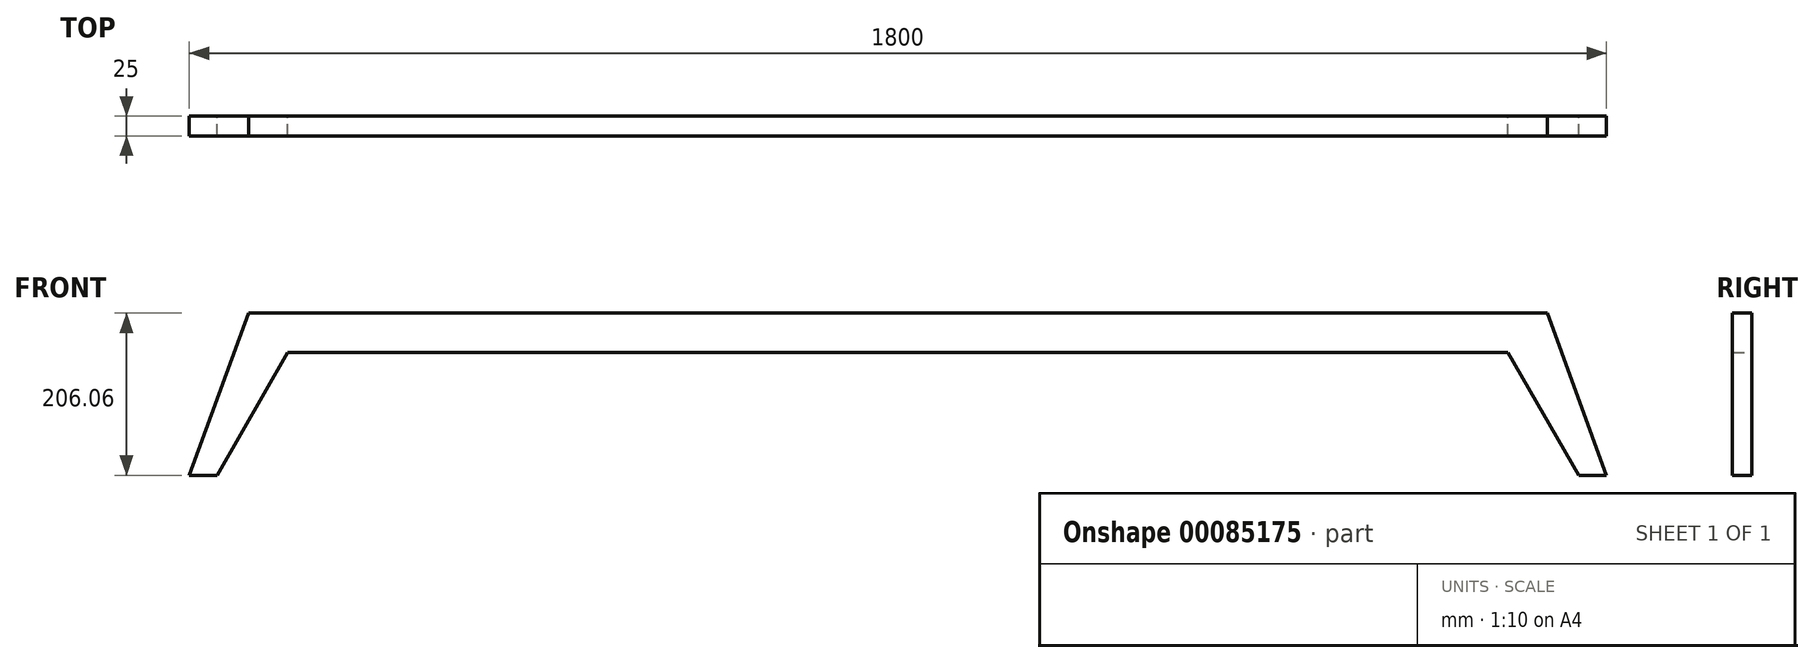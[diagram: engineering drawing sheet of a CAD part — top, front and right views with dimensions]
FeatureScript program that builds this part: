
annotation { "Feature Type Name" : "Feature", "Feature Type Description" : "" }
export const myFeature = defineFeature(function(context is Context, id is Id, definition is map)
    precondition{}
    {
        {
            var Q0;
            Q0=qCreatedBy(makeId("Front.planeOp"),FACE);
            var sketch = newSketch(context, id + "F0", { "sketchPlane" : qUnion([Q0])});
            skLineSegment(sketch, "E0", {"start": v(0, 0) * mm, "end": v(-825, 0) * mm});
            skLineSegment(sketch, "E1", {"start": v(-825, 0) * mm, "end": v(-900, -206.06) * mm});
            skLineSegment(sketch, "E2", {"start": v(-900, -206.06) * mm, "end": v(-865, -206.06) * mm});
            skLineSegment(sketch, "E3", {"start": v(-865, -206.06) * mm, "end": v(-775, -50.18) * mm});
            skLineSegment(sketch, "E4", {"start": v(-775, -50.18) * mm, "end": v(0, -50.18) * mm});
            skLineSegment(sketch, "E5", {"start": v(0, -50.18) * mm, "end": v(0, 0) * mm});
            skLineSegment(sketch, "E6.MirrorCS", {"start": v(900, -206.06) * mm, "end": v(865, -206.06) * mm});
            skLineSegment(sketch, "E7.MirrorCS", {"start": v(825, 0) * mm, "end": v(900, -206.06) * mm});
            skLineSegment(sketch, "E8.MirrorCS", {"start": v(865, -206.06) * mm, "end": v(775, -50.18) * mm});
            skLineSegment(sketch, "E9.MirrorCS", {"start": v(775, -50.18) * mm, "end": v(0, -50.18) * mm});
            skLineSegment(sketch, "E10.MirrorCS", {"start": v(0, 0) * mm, "end": v(825, 0) * mm});
            skSolve(sketch);
        }
        {
            var Q0;
            Q0 = qSketchRegion(id + "F0", true);
            extrude(context, id + "F1", {"entities" : qUnion([Q0]), "depth" : 25 * mm});
        }
    });
